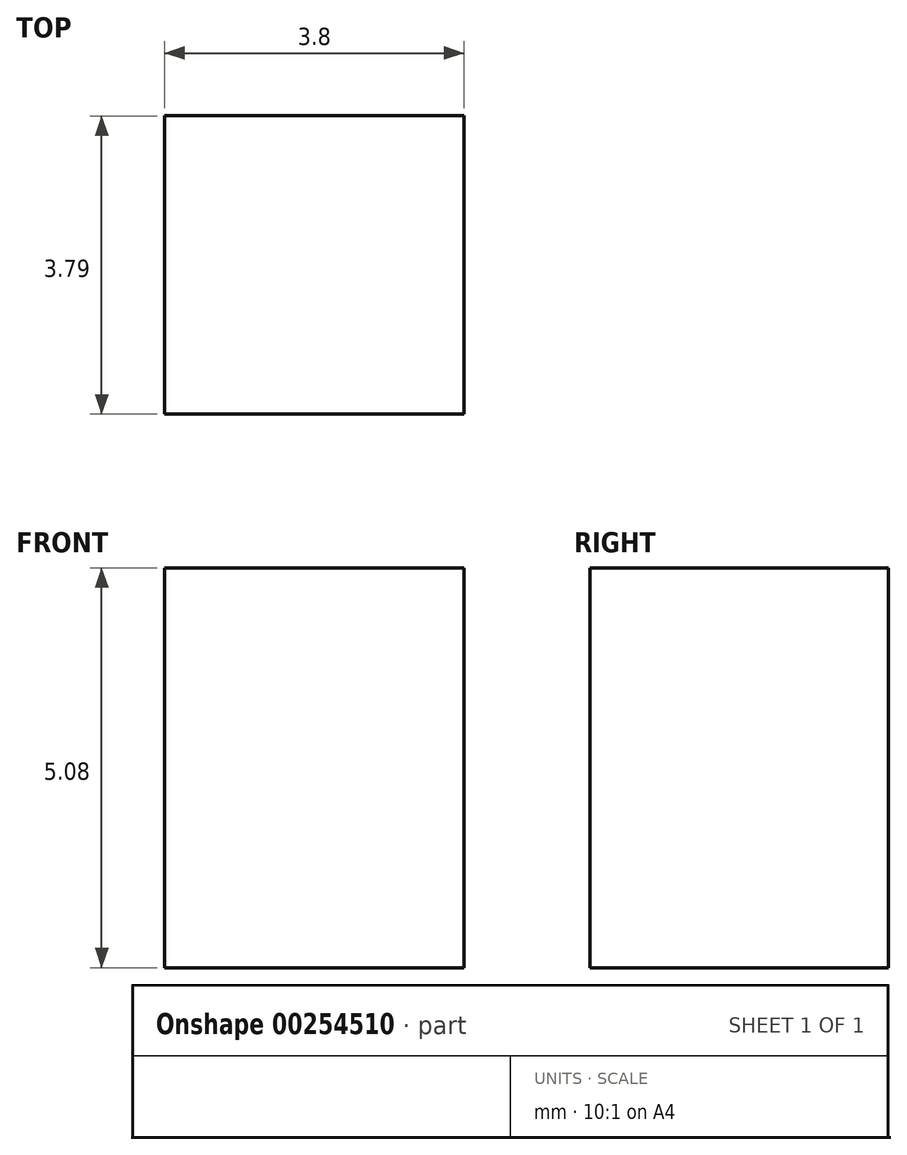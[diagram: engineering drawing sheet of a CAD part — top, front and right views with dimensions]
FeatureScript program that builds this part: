
annotation { "Feature Type Name" : "Feature", "Feature Type Description" : "" }
export const myFeature = defineFeature(function(context is Context, id is Id, definition is map)
    precondition{}
    {
        {
            var Q0;
            Q0=qCreatedBy(makeId("Top.planeOp"),FACE);
            var sketch = newSketch(context, id + "F0", { "sketchPlane" : qUnion([Q0])});
            skLineSegment(sketch, "E0", {"start": v(-33.45, 9.2) * mm, "end": v(-26.8, 16.12) * mm});
            skLineSegment(sketch, "E1", {"start": v(-26.8, 16.12) * mm, "end": v(-22.17, 16.12) * mm});
            skLineSegment(sketch, "E2", {"start": v(-22.17, 16.12) * mm, "end": v(-22.17, 19.99) * mm});
            skLineSegment(sketch, "E3", {"start": v(-22.17, 19.99) * mm, "end": v(-25.8, 19.97) * mm});
            skLineSegment(sketch, "E4", {"start": v(-25.8, 19.97) * mm, "end": v(-25.8, 38.73) * mm});
            skLineSegment(sketch, "E5", {"start": v(-25.8, 38.73) * mm, "end": v(-18.88, 45.9) * mm});
            skLineSegment(sketch, "E6", {"start": v(-18.88, 45.9) * mm, "end": v(14.3, 45.9) * mm});
            skLineSegment(sketch, "E7", {"start": v(14.3, 45.9) * mm, "end": v(22.2, 38.73) * mm});
            skLineSegment(sketch, "E8", {"start": v(22.2, 38.73) * mm, "end": v(22.2, 19.97) * mm});
            skLineSegment(sketch, "E9", {"start": v(22.2, 19.97) * mm, "end": v(18.52, 19.97) * mm});
            skLineSegment(sketch, "E10", {"start": v(18.52, 19.97) * mm, "end": v(18.52, 16.12) * mm});
            skLineSegment(sketch, "E11", {"start": v(18.52, 16.12) * mm, "end": v(22.2, 16.12) * mm});
            skLineSegment(sketch, "E12", {"start": v(22.2, 16.12) * mm, "end": v(29.83, 9.43) * mm});
            skLineSegment(sketch, "E13", {"start": v(29.83, 9.43) * mm, "end": v(29.83, -20.85) * mm});
            skLineSegment(sketch, "E14", {"start": v(29.83, -20.85) * mm, "end": v(22.14, -20.85) * mm});
            skLineSegment(sketch, "E15", {"start": v(22.14, -20.85) * mm, "end": v(22.14, -32.04) * mm});
            skLineSegment(sketch, "E16", {"start": v(22.14, -32.04) * mm, "end": v(19.03, -35.7) * mm});
            skLineSegment(sketch, "E17", {"start": v(19.03, -35.7) * mm, "end": v(3.87, -35.7) * mm});
            skLineSegment(sketch, "E18", {"start": v(3.87, -35.7) * mm, "end": v(3.87, -28.47) * mm});
            skLineSegment(sketch, "E19", {"start": v(3.87, -28.47) * mm, "end": v(-7.29, -28.47) * mm});
            skLineSegment(sketch, "E20", {"start": v(-7.29, -28.47) * mm, "end": v(-7.29, -35.7) * mm});
            skLineSegment(sketch, "E21", {"start": v(-7.29, -35.7) * mm, "end": v(-23.05, -35.7) * mm});
            skLineSegment(sketch, "E22", {"start": v(-23.05, -35.7) * mm, "end": v(-25.8, -32.44) * mm});
            skLineSegment(sketch, "E23", {"start": v(-25.8, -32.44) * mm, "end": v(-25.8, -20.85) * mm});
            skLineSegment(sketch, "E24", {"start": v(-25.8, -20.85) * mm, "end": v(-33.32, -20.85) * mm});
            skLineSegment(sketch, "E25", {"start": v(-33.32, -20.85) * mm, "end": v(-33.45, 9.2) * mm});
            skCircle(sketch, "E26", {"center": v(-11.3, 31.23) * mm, "radius": 5.9 * mm});
            skPoint(sketch, "E26.first.point", {"position": v(-17.19, 30.94) * mm});
            skPoint(sketch, "E26.second.point", {"position": v(-5.4, 31.07) * mm});
            skPoint(sketch, "E26.third.point", {"position": v(-11.26, 25.33) * mm});
            skCircle(sketch, "E27", {"center": v(7.12, 31) * mm, "radius": 5.64 * mm});
            skPoint(sketch, "E27.first.point", {"position": v(1.48, 30.84) * mm});
            skPoint(sketch, "E27.second.point", {"position": v(12.76, 30.78) * mm});
            skPoint(sketch, "E27.third.point", {"position": v(7.1, 36.64) * mm});
            skLineSegment(sketch, "E28.bottom", {"start": v(-14.96, 34.57) * mm, "end": v(-7.5, 34.57) * mm});
            skLineSegment(sketch, "E28.top", {"start": v(-14.96, 27.44) * mm, "end": v(-7.5, 27.44) * mm});
            skLineSegment(sketch, "E28.left", {"start": v(-14.96, 34.57) * mm, "end": v(-14.96, 27.44) * mm});
            skLineSegment(sketch, "E28.right", {"start": v(-7.5, 34.57) * mm, "end": v(-7.5, 27.44) * mm});
            skLineSegment(sketch, "E29.bottom", {"start": v(3.8, 34.28) * mm, "end": v(10.72, 34.28) * mm});
            skLineSegment(sketch, "E29.top", {"start": v(3.8, 27.44) * mm, "end": v(10.72, 27.44) * mm});
            skLineSegment(sketch, "E29.left", {"start": v(3.8, 34.28) * mm, "end": v(3.8, 27.44) * mm});
            skLineSegment(sketch, "E29.right", {"start": v(10.72, 34.28) * mm, "end": v(10.72, 27.44) * mm});
            skLineSegment(sketch, "E30.bottom", {"start": v(7.12, 31) * mm, "end": v(3.8, 31) * mm});
            skLineSegment(sketch, "E30.top", {"start": v(7.12, 34.28) * mm, "end": v(3.8, 34.28) * mm});
            skLineSegment(sketch, "E30.left", {"start": v(7.12, 31) * mm, "end": v(7.12, 34.28) * mm});
            skLineSegment(sketch, "E30.right", {"start": v(3.8, 31) * mm, "end": v(3.8, 34.28) * mm});
            skLineSegment(sketch, "E31.bottom", {"start": v(-11.3, 31.23) * mm, "end": v(-14.96, 31.23) * mm});
            skLineSegment(sketch, "E31.top", {"start": v(-11.3, 34.57) * mm, "end": v(-14.96, 34.57) * mm});
            skLineSegment(sketch, "E31.left", {"start": v(-11.3, 31.23) * mm, "end": v(-11.3, 34.57) * mm});
            skLineSegment(sketch, "E31.right", {"start": v(-14.96, 31.23) * mm, "end": v(-14.96, 34.57) * mm});
            skLineSegment(sketch, "E32.bottom", {"start": v(-3.8, 23.6) * mm, "end": v(0, 23.6) * mm});
            skLineSegment(sketch, "E32.top", {"start": v(-3.8, 19.8) * mm, "end": v(0, 19.8) * mm});
            skLineSegment(sketch, "E32.left", {"start": v(-3.8, 23.6) * mm, "end": v(-3.8, 19.8) * mm});
            skLineSegment(sketch, "E32.right", {"start": v(0, 23.6) * mm, "end": v(0, 19.8) * mm});
            skLineSegment(sketch, "E33.bottom", {"start": v(-7.5, 15.86) * mm, "end": v(3.8, 15.86) * mm});
            skLineSegment(sketch, "E33.top", {"start": v(-7.5, 12.27) * mm, "end": v(3.8, 12.27) * mm});
            skLineSegment(sketch, "E33.left", {"start": v(-7.5, 15.86) * mm, "end": v(-7.5, 12.27) * mm});
            skLineSegment(sketch, "E33.right", {"start": v(3.8, 15.86) * mm, "end": v(3.8, 12.27) * mm});
            skPoint(sketch, "E34.oppositeSnap0", {"position": v(-25.8, -26.64) * mm});
            skLineSegment(sketch, "E34.bottom", {"start": v(-29.45, -9.9) * mm, "end": v(-25.8, -9.9) * mm});
            skLineSegment(sketch, "E34.top", {"start": v(-29.45, -17.27) * mm, "end": v(-25.8, -17.27) * mm});
            skLineSegment(sketch, "E34.left", {"start": v(-29.45, -9.9) * mm, "end": v(-29.45, -17.27) * mm});
            skLineSegment(sketch, "E34.right", {"start": v(-25.8, -9.9) * mm, "end": v(-25.8, -17.27) * mm});
            skLineSegment(sketch, "E35.top", {"start": v(-29.45, 8.74) * mm, "end": v(-25.8, 8.74) * mm});
            skLineSegment(sketch, "E35.left", {"start": v(-29.45, -9.9) * mm, "end": v(-29.45, 8.74) * mm});
            skLineSegment(sketch, "E35.right", {"start": v(-25.8, -9.9) * mm, "end": v(-25.8, 8.74) * mm});
            skLineSegment(sketch, "E36.bottom", {"start": v(22.2, -9.9) * mm, "end": v(25.76, -9.9) * mm});
            skLineSegment(sketch, "E36.top", {"start": v(22.2, -17.27) * mm, "end": v(25.76, -17.27) * mm});
            skLineSegment(sketch, "E36.left", {"start": v(22.2, -9.9) * mm, "end": v(22.2, -17.27) * mm});
            skLineSegment(sketch, "E36.right", {"start": v(25.76, -9.9) * mm, "end": v(25.76, -17.27) * mm});
            skLineSegment(sketch, "E37.top", {"start": v(22.2, 8.7) * mm, "end": v(25.76, 8.7) * mm});
            skLineSegment(sketch, "E37.left", {"start": v(22.2, -9.9) * mm, "end": v(22.2, 8.7) * mm});
            skLineSegment(sketch, "E37.right", {"start": v(25.76, -9.9) * mm, "end": v(25.76, 8.7) * mm});
            skLineSegment(sketch, "E38.bottom", {"start": v(-3.6, -28.47) * mm, "end": v(0, -28.47) * mm});
            skLineSegment(sketch, "E38.top", {"start": v(-3.6, -24.74) * mm, "end": v(0, -24.74) * mm});
            skLineSegment(sketch, "E38.left", {"start": v(-3.6, -28.47) * mm, "end": v(-3.6, -24.74) * mm});
            skLineSegment(sketch, "E38.right", {"start": v(0, -28.47) * mm, "end": v(0, -24.74) * mm});
            skLineSegment(sketch, "E39", {"start": v(-22.24, -24.61) * mm, "end": v(-22.24, -31.85) * mm});
            skLineSegment(sketch, "E40", {"start": v(-22.24, -31.85) * mm, "end": v(-11.06, -31.85) * mm});
            skLineSegment(sketch, "E41", {"start": v(-11.06, -31.85) * mm, "end": v(-11.06, -28.48) * mm});
            skLineSegment(sketch, "E42", {"start": v(-11.06, -28.48) * mm, "end": v(-7.29, -28.47) * mm});
            skLineSegment(sketch, "E43", {"start": v(-7.29, -24.61) * mm, "end": v(-22.24, -24.61) * mm});
            skLineSegment(sketch, "E44", {"start": v(-7.29, -24.61) * mm, "end": v(-7.29, -28.47) * mm});
            skLineSegment(sketch, "E45", {"start": v(3.87, -28.47) * mm, "end": v(3.87, -24.61) * mm});
            skLineSegment(sketch, "E46", {"start": v(3.87, -24.61) * mm, "end": v(18.56, -24.61) * mm});
            skLineSegment(sketch, "E47", {"start": v(18.56, -24.61) * mm, "end": v(18.56, -31.97) * mm});
            skLineSegment(sketch, "E48", {"start": v(18.56, -31.97) * mm, "end": v(7.4, -31.97) * mm});
            skLineSegment(sketch, "E49", {"start": v(7.4, -31.97) * mm, "end": v(7.4, -28.47) * mm});
            skLineSegment(sketch, "E50", {"start": v(7.4, -28.47) * mm, "end": v(3.87, -28.47) * mm});
            skLineSegment(sketch, "E51", {"start": v(-22.17, 19.99) * mm, "end": v(-22.24, 38.23) * mm});
            skLineSegment(sketch, "E52", {"start": v(-22.24, 38.23) * mm, "end": v(-18.48, 38.25) * mm});
            skLineSegment(sketch, "E53", {"start": v(-18.48, 38.25) * mm, "end": v(-18.5, 42.04) * mm});
            skLineSegment(sketch, "E54", {"start": v(-18.5, 42.04) * mm, "end": v(14.76, 42.16) * mm});
            skLineSegment(sketch, "E55", {"start": v(14.76, 42.16) * mm, "end": v(14.78, 38.23) * mm});
            skLineSegment(sketch, "E56", {"start": v(14.78, 38.23) * mm, "end": v(18.52, 38.24) * mm});
            skLineSegment(sketch, "E57", {"start": v(18.52, 38.24) * mm, "end": v(18.52, 19.97) * mm});
            skLineSegment(sketch, "E58", {"start": v(3.8, 15.86) * mm, "end": v(3.8, 19.97) * mm});
            skLineSegment(sketch, "E59", {"start": v(3.8, 19.97) * mm, "end": v(18.52, 19.97) * mm});
            skLineSegment(sketch, "E60", {"start": v(-7.5, 15.86) * mm, "end": v(-7.5, 19.99) * mm});
            skLineSegment(sketch, "E61", {"start": v(-7.5, 19.99) * mm, "end": v(-22.17, 19.99) * mm});
            skLineSegment(sketch, "E62", {"start": v(-22.23, 12.38) * mm, "end": v(-22.23, -21.38) * mm});
            skLineSegment(sketch, "E63", {"start": v(-22.23, -21.38) * mm, "end": v(18.48, -21.38) * mm});
            skLineSegment(sketch, "E64", {"start": v(18.48, -21.38) * mm, "end": v(18.48, 12.34) * mm});
            skLineSegment(sketch, "E65", {"start": v(18.48, 12.34) * mm, "end": v(14.65, 12.34) * mm});
            skLineSegment(sketch, "E66", {"start": v(14.65, 12.34) * mm, "end": v(14.65, 15.86) * mm});
            skLineSegment(sketch, "E67", {"start": v(14.65, 15.86) * mm, "end": v(3.8, 15.86) * mm});
            skLineSegment(sketch, "E68", {"start": v(-22.23, 12.38) * mm, "end": v(-18.53, 12.38) * mm});
            skLineSegment(sketch, "E69", {"start": v(-18.53, 12.38) * mm, "end": v(-18.53, 15.86) * mm});
            skLineSegment(sketch, "E70", {"start": v(-18.53, 15.86) * mm, "end": v(-7.5, 15.86) * mm});
            skLineSegment(sketch, "E71.bottom", {"start": v(-7.42, -28.31) * mm, "end": v(-7.13, -28.31) * mm});
            skLineSegment(sketch, "E71.top", {"start": v(-7.42, -28.63) * mm, "end": v(-7.13, -28.63) * mm});
            skLineSegment(sketch, "E71.left", {"start": v(-7.42, -28.31) * mm, "end": v(-7.42, -28.63) * mm});
            skLineSegment(sketch, "E71.right", {"start": v(-7.13, -28.31) * mm, "end": v(-7.13, -28.63) * mm});
            skLineSegment(sketch, "E72.bottom", {"start": v(3.95, -28.38) * mm, "end": v(3.78, -28.38) * mm});
            skLineSegment(sketch, "E72.top", {"start": v(3.95, -28.56) * mm, "end": v(3.78, -28.56) * mm});
            skLineSegment(sketch, "E72.left", {"start": v(3.95, -28.38) * mm, "end": v(3.95, -28.56) * mm});
            skLineSegment(sketch, "E72.right", {"start": v(3.78, -28.38) * mm, "end": v(3.78, -28.56) * mm});
            skSolve(sketch);
        }
        {
            var Q0;
            Q0=makeQuery(id+"F0.imprint","IMPRINT",FACE,{"disambiguationData":[TD([[makeQuery(id+"F0.imprint","IMPRINT",EDGE,{"derivedFrom":sQuery(id+"F0.wireOp",EDGE,"E32.bottom")}),-1.0]])]});
            extrude(context, id + "F1", {"entities" : qUnion([Q0]), "depth" : 5.08 * mm});
        }
    });
